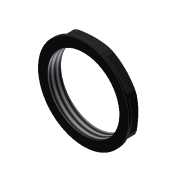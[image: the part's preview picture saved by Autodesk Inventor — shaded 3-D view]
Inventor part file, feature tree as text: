
AUTODESK INVENTOR PART (.ipt)
format: ipt  version: 2014 SP1 (Build 180222100, 222)  size: 107,520 bytes
history: native  units: mm
features: imported_body x1, thread x1
ambient origin geometry x8: Origin, YZ Plane, XZ Plane, XY Plane, X Axis, Y Axis, Z Axis, Center Point
bodies: Solid1 (feature_tree)
feature tree (2):
  imported_body  "Base1"
  thread  "Thread1"  [1 undecoded]
note: 1 required parameter value undecoded (feature->parameter linkage not recoverable at this tier; creation-order binding heuristic only, values carry confidence <= 0.55)
